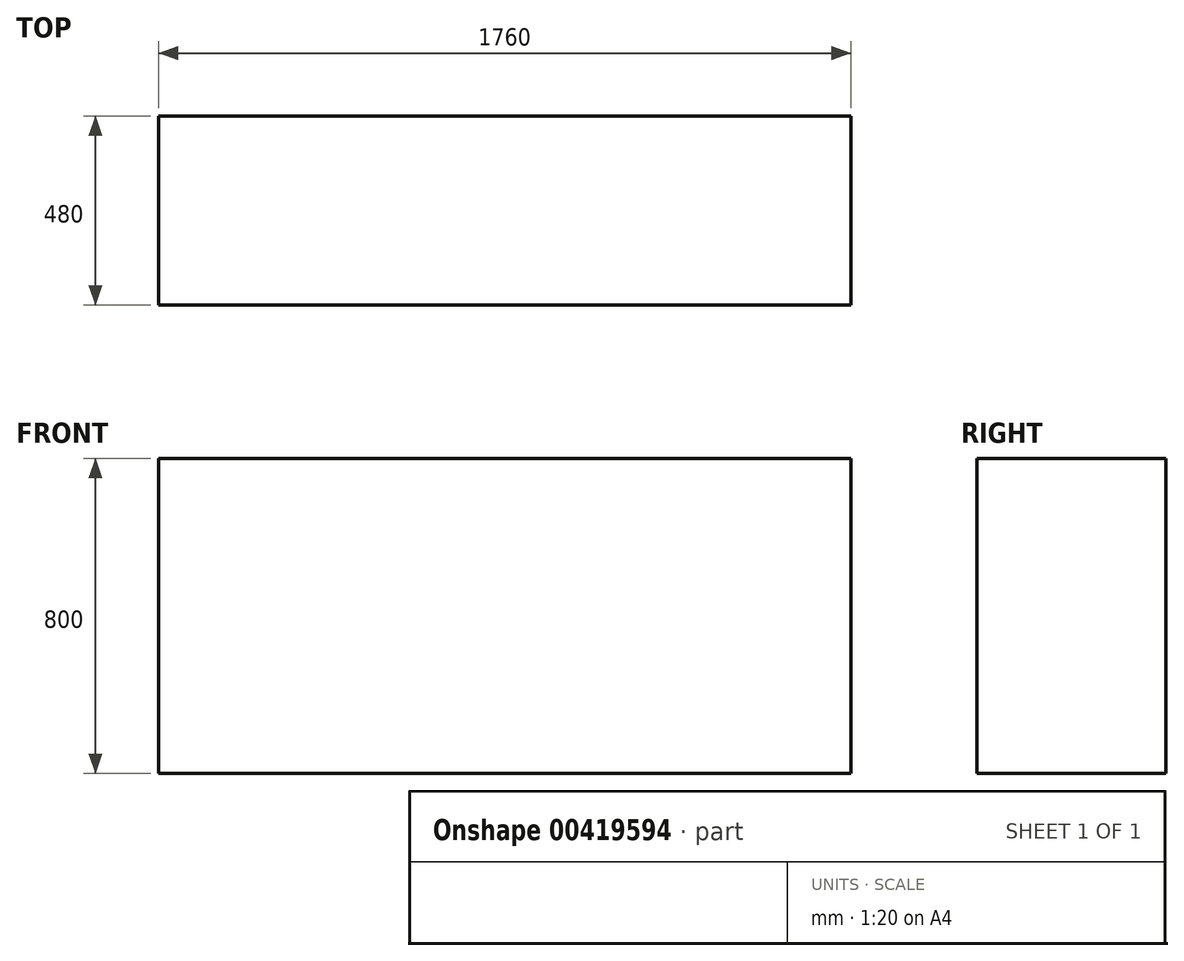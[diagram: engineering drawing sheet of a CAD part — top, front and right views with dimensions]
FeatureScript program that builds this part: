
annotation { "Feature Type Name" : "Feature", "Feature Type Description" : "" }
export const myFeature = defineFeature(function(context is Context, id is Id, definition is map)
    precondition{}
    {
        {
            var Q0;
            Q0=qCreatedBy(makeId("Top.planeOp"),FACE);
            var sketch = newSketch(context, id + "F0", { "sketchPlane" : qUnion([Q0])});
            skLineSegment(sketch, "E0.bottom", {"start": v(-1623.83, 420.26) * mm, "end": v(136.17, 420.26) * mm});
            skLineSegment(sketch, "E0.top", {"start": v(-1623.83, -59.74) * mm, "end": v(136.17, -59.74) * mm});
            skLineSegment(sketch, "E0.left", {"start": v(-1623.83, 420.26) * mm, "end": v(-1623.83, -59.74) * mm});
            skLineSegment(sketch, "E0.right", {"start": v(136.17, 420.26) * mm, "end": v(136.17, -59.74) * mm});
            skSolve(sketch);
        }
        {
            var Q0;
            Q0=makeQuery(id+"F0.imprint","IMPRINT",FACE,{"disambiguationData":[TD([[makeQuery(id+"F0.imprint","IMPRINT",EDGE,{"derivedFrom":sQuery(id+"F0.wireOp",EDGE,"E0.bottom")}),-1.0]])]});
            extrude(context, id + "F1", {"entities" : qUnion([Q0]), "depth" : 800 * mm});
        }
    });
